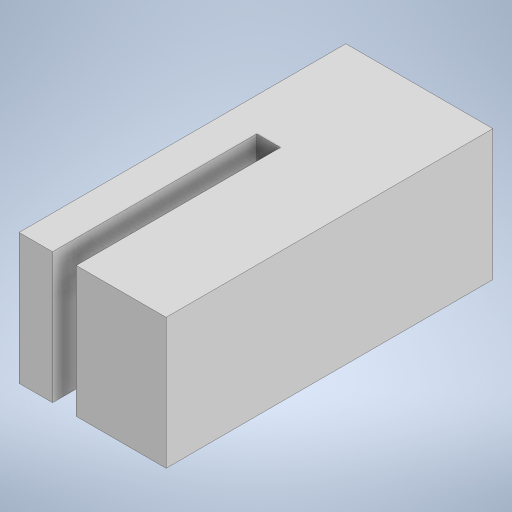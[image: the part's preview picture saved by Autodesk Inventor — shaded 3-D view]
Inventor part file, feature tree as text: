
AUTODESK INVENTOR PART (.ipt)
format: ipt  version: 2023 (Build 270158000, 158)  size: 189,952 bytes
history: native  units: in
note: dims shown in document units (in); Inventor stores cm internally (conversion verified against a paired STEP export)
features: extrude x2, sketch x2
ambient origin geometry x8: Origin, YZ Plane, XZ Plane, XY Plane, X Axis, Y Axis, Z Axis, Center Point
bodies: Solid1 (feature_tree)
feature tree (4):
  extrude  "Extrusion1"  Depth=1.0in
  extrude  "Extrusion2"  Depth=0.275in
  sketch  "Sketch1"  dims[d0=0.45in d1=1.0in]
  sketch  "Sketch2"  dims[d2=0.4in d3=0.0in d4=0.275in d5=0.0725in d6=0.625in d7=0.5in d8=0.0in]
